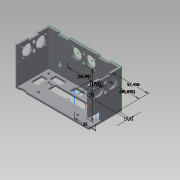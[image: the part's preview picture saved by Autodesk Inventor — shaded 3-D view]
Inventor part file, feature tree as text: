
AUTODESK INVENTOR PART (.ipt)
format: ipt  version: 2015 SP1 (Build 190203100, 203)  size: 480,256 bytes
history: native  units: mm
features: sketch x19, extrude x18, projected_geometry x4, fillet x1, plane x1, chamfer x1
ambient origin geometry x8: Origin, YZ Plane, XZ Plane, XY Plane, X Axis, Y Axis, Z Axis, Center Point
bodies: Body1 (feature_tree)
feature tree (44):
  sketch  "Sketch1"  dims[d49=120.812mm d51=3.0mm]
  extrude  "Extrusion5"  Depth=3.0mm
  extrude  "Extrusion6"  Depth=60.0mm TaperAngle=0.0deg
  extrude  "Extrusion7"  Depth=3.0mm
  extrude  "Extrusion8"  Depth=51.214111mm
  extrude  "Extrusion9"  Depth=10.0mm TaperAngle=0.0deg
  extrude  "Extrusion10"  Depth=17.5mm
  sketch  "Sketch12"  dims[d65=10.0mm d66=17.5mm]
  extrude  "Extrusion11"  Depth=10.0mm TaperAngle=0.0deg
  extrude  "Extrusion12"  Depth=10.0mm TaperAngle=0.0deg
  fillet  "Fillet2"  Radius=22.0mm
  extrude  "Extrusion13"  Depth=15.0mm
  plane  "Work Plane1"
  sketch  "Sketch20"  dims[d80=3.0mm d81=0.0mm d82=10.0mm d83=0.0mm d84=22.0mm]
  extrude  "Extrusion24"  Depth=10.0mm TaperAngle=0.0deg
  extrude  "Extrusion25"  Depth=2.0mm
  extrude  "Extrusion26"  Depth=3.5mm
  extrude  "Extrusion27"  Depth=20.0mm
  extrude  "Extrusion28"  Depth=3.5mm
  extrude  "Extrusion29"  Depth=10.0mm
  extrude  "Extrusion30"  Depth=10.0mm TaperAngle=0.0deg
  chamfer  "Chamfer1"  Distance=10.0mm
  extrude  "Extrusion31"  Depth=10.0mm TaperAngle=0.0deg
  extrude  "Extrusion32"  Depth=7.5mm
  sketch  "Sketch36"  dims[d167=180.0deg d168=7.5mm]
  sketch  "Sketch37"  dims[d169=7.5mm d170=10.0mm d171=0.0mm d172=22.5mm d173=3.0mm d174=22.5mm d175=15.0mm d176=0.0mm d177=7.5mm d178=7.5mm d179=15.0mm d180=0.0mm d187=2.0mm d188=3.0mm d189=6.5mm d190=2.0mm d191=3.0mm d192=6.5mm d193=2.0mm d194=3.0mm d195=2.0mm d196=3.0mm d197=6.5mm d198=6.5mm d199=0.5mm d200=15.0mm d201=0.0mm d202=5.0mm d203=2.0mm d204=45.0deg d223=10.0mm d224=0.0mm d225=17.5mm d226=10.0mm d227=17.5mm d228=6.0mm d229=10.0mm d230=0.0mm d231=3.6mm d232=48.656mm d233=17.5mm d234=57.406mm d235=56.99mm d236=75.0mm d237=35.0mm]
  sketch  "Sketch6"  dims[d52=3.0mm d53=0.0mm d54=60.0mm d55=0.0mm]
  sketch  "Sketch7"  dims[d57=3.0mm d58=3.0mm]
  sketch  "Sketch9"  dims[d59=114.812mm d61=51.214111mm]
  sketch  "Sketch10"  dims[d62=3.5mm d63=10.0mm d64=0.0mm]
  sketch  "Sketch13"  dims[d69=10.0mm d72=10.0mm d73=0.0mm]
  sketch  "Sketch22"  dims[d85=22.0mm d86=15.0mm]
  sketch  "Sketch23"  dims[d87=10.0mm d88=200.0mm d89=0.0mm]
  sketch  "Sketch24"  dims[d90=200.0mm d91=0.0mm d92=2.0mm]
  sketch  "Sketch25"  dims[d95=3.5mm d96=3.5mm]
  sketch  "Sketch26"  dims[d97=3.5mm d99=20.0mm]
  sketch  "Sketch27"  dims[d100=55.0mm d101=3.5mm]
  projected_geometry  "Projected Loop1"
  projected_geometry  "Projected Loop2"
  sketch  "Sketch30"  dims[d102=10.0mm d103=0.0mm d121=19.75mm]
  sketch  "Sketch34"  dims[d132=6.5mm d160=10.0mm d161=0.0mm d162=10.0mm d163=0.0mm]
  projected_geometry  "Projected Loop6"
  sketch  "Sketch35"  dims[d164=17.5mm d165=10.0mm d166=0.0mm]
  projected_geometry  "Projected Loop7"
